# Revit family: hd250e  with pipe cover(1)
name_source: partatom
category: Generic Models
units: mm (PartAtom-declared; Revit-internal decimal feet)

## family parameters
Can host rebar = No
Cut with Voids When Loaded = No
Host = Face
Part Type = Normal
Room Calculation Point = No
Round Connector Dimension = Use Diameter
Shared = No

## types (2) — shared parameters
Cold Water Connection = R¾ (20mm)
Cold Water Connection (from centreline) = 52 mm
Cold Water Connection (from wall) = 99 mm
Default Elevation = 1219 mm
Gas Connection = R¾ (20mm)
Gas Connection (from centreline) = 110 mm
Gas Connection (from wall) = 61 mm
Gas consumption = 249 MJ/h
Hot Water Capacity = 3.2 -37 L/min
Hot Water Capacity @25 deg rise = 32 L/min
Hot Water Connection = R¾ (20mm)
Hot Water Connection (from centreline) = 61 mm
Hot Water Connection (from wall) = 115 mm
Ingress Protection Rating = IPX4
Input = 20-249 MJ/h
Manufacturer = Rinnai
Noise Level (1m away) = 50 dB (A)
Nominal Operating Pressure = 200 - 1000kPa
Ouput = 57.8kW
Power Consumption (automatic frost protection) = 116 W
Power Consumption (normal) = 72 W
Power Consumption (standby) = 2 W
Thermal Efficiency (on high) = 83%
URL = https://rinnai.co.nz
Weight = 29 kg

## per-type parameters (varying)
| type | Description |
| INFHD250HNCN | Infinity HD250 (NG) - EXTERNAL ONLY |
| INFHD250HNCL | Infinity HD250 (LPG) - EXTERNAL ONLY |

note: column(s) folded — value = type name in every type: Model

## geometry (parser evidence)
native form markers: Sweep x1
no freeform markers — native parametric forms only
